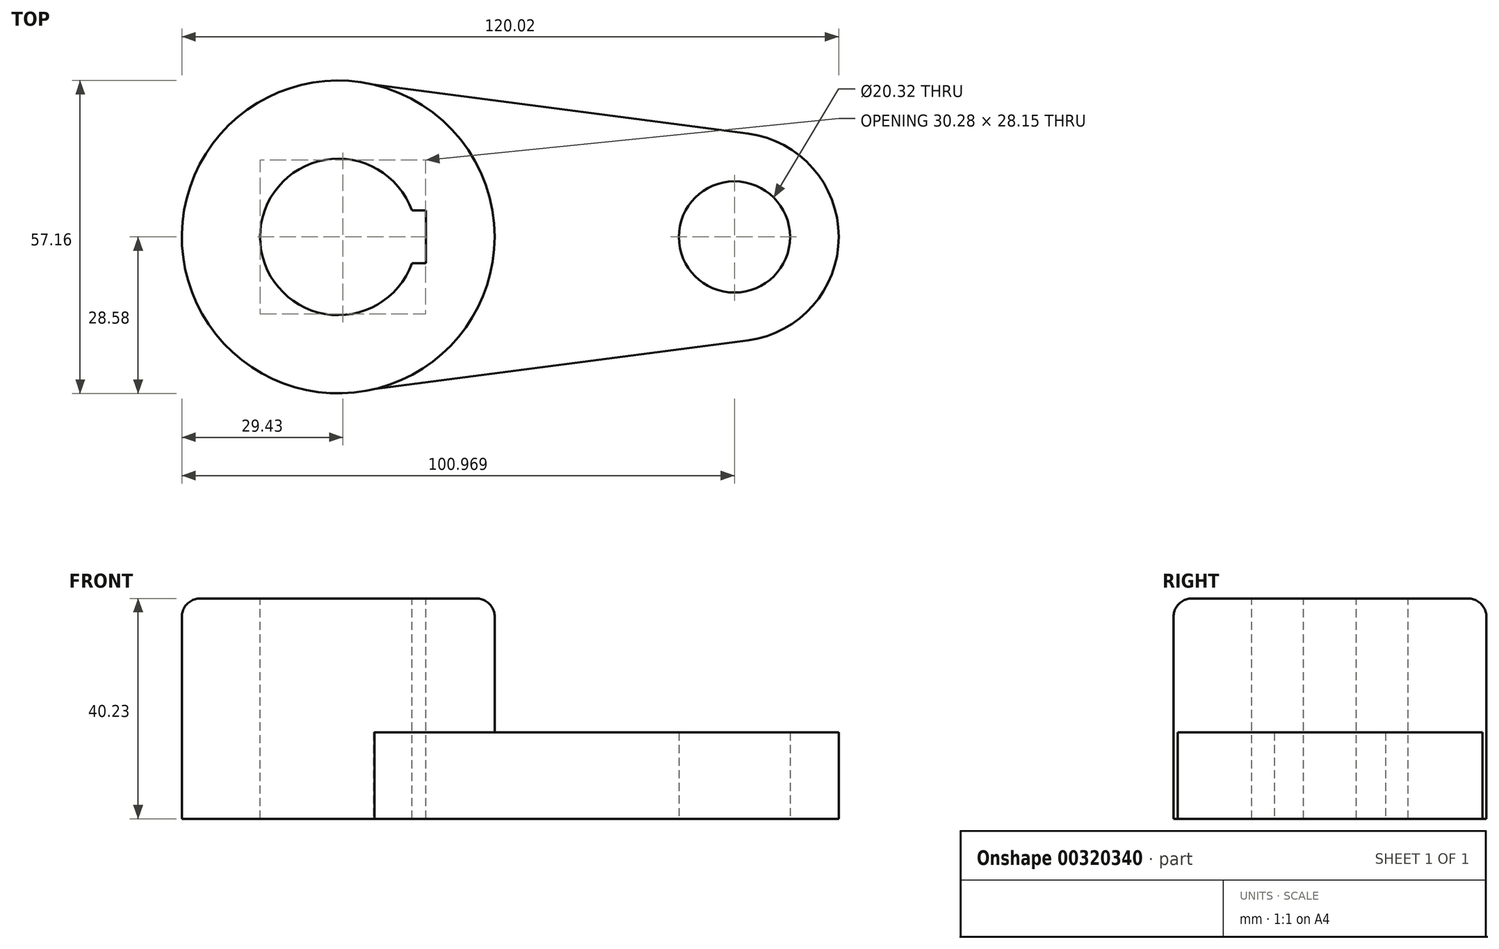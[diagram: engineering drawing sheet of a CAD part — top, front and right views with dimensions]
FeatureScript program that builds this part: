
annotation { "Feature Type Name" : "Feature", "Feature Type Description" : "" }
export const myFeature = defineFeature(function(context is Context, id is Id, definition is map)
    precondition{}
    {
        {
            var Q0;
            Q0=qCreatedBy(makeId("Top.planeOp"),FACE);
            var sketch = newSketch(context, id + "F0", { "sketchPlane" : qUnion([Q0])});
            skCircle(sketch, "E0", {"center": v(41.53, 0) * mm, "radius": 19.05 * mm});
            skCircle(sketch, "E1", {"center": v(-30.86, 0) * mm, "radius": 28.58 * mm});
            skLineSegment(sketch, "E2", {"start": v(-29.88, 28.56) * mm, "end": v(44, 18.89) * mm});
            skLineSegment(sketch, "E3", {"start": v(-30.11, -28.57) * mm, "end": v(44, -18.89) * mm});
            skSolve(sketch);
        }
        {
            var Q0;
            Q0 = qSketchRegion(id + "F0", true);
            extrude(context, id + "F1", {"entities" : qUnion([Q0]), "depth" : 15.77 * mm});
        }
        {
            var Q0;
            Q0=qCreatedBy(makeId("Top.planeOp"),FACE);
            var sketch = newSketch(context, id + "F2", { "sketchPlane" : qUnion([Q0])});
            skArc(sketch, "E4.0", {"start": v(-24.46, 27.85) * mm, "mid": v(-59.44, -0.1) * mm, "end": v(-24.25, -27.8) * mm});
            skArc(sketch, "E5.0.0", {"start": v(44, -18.89) * mm, "mid": v(60.58, 0) * mm, "end": v(44, 18.89) * mm, "construction": true});
            skLineSegment(sketch, "E5.0.1", {"start": v(44, 18.89) * mm, "end": v(-24.46, 27.85) * mm, "construction": true});
            skArc(sketch, "E5.0.2", {"start": v(-24.46, 27.85) * mm, "mid": v(-59.44, -0.1) * mm, "end": v(-24.25, -27.8) * mm, "construction": true});
            skLineSegment(sketch, "E5.0.3", {"start": v(-24.25, -27.8) * mm, "end": v(44, -18.89) * mm, "construction": true});
            skCircle(sketch, "E6", {"center": v(-30.86, 0) * mm, "radius": 28.57 * mm});
            skSolve(sketch);
        }
        {
            var Q0;
            Q0 = qSketchRegion(id + "F2", true);
            extrude(context, id + "F3", {"entities" : qUnion([Q0]), "operationType" : NewBodyOperationType.ADD, "depth" : 40.23 * mm});
        }
        {
            var Q0;
            Q0=makeQuery(id+"F3.opExtrude","CAP_EDGE",EDGE,{"disambiguationData":[OSD([sQuery(id+"F2.wireOp",EDGE,"E6")])],"isStart":false});
            fillet(context, id + "F4", {"entities" : qUnion([Q0]), "radius" : 3.3 * mm, "tangentPropagation" : true, "allowEdgeOverflow" : false});
        }
        {
            var Q0;
            Q0=qCreatedBy(makeId("Top.planeOp"),FACE);
            var sketch = newSketch(context, id + "F5", { "sketchPlane" : qUnion([Q0])});
            skArc(sketch, "E7.0", {"start": v(44, -18.89) * mm, "mid": v(60.58, 0) * mm, "end": v(44, 18.89) * mm, "construction": true});
            skCircle(sketch, "E8", {"center": v(41.53, 0) * mm, "radius": 10.16 * mm});
            skSolve(sketch);
        }
        {
            var Q0;
            Q0 = qSketchRegion(id + "F5", true);
            extrude(context, id + "F6", {"entities" : qUnion([Q0]), "operationType" : NewBodyOperationType.REMOVE, "endBound" : BoundingType.THROUGH_ALL, "depth" : 25.4 * mm});
        }
        {
            var Q0;
            Q0=makeQuery(id+"F3.opExtrude","CAP_FACE",FACE,{"disambiguationData":[OSD([sQuery(id+"F2.wireOp",EDGE,"E6")])],"isStart":false});
            var sketch = newSketch(context, id + "F7", { "sketchPlane" : qUnion([Q0])});
            skCircle(sketch, "E9.0.0", {"center": v(-30.86, 0) * mm, "radius": 25.27 * mm, "construction": true});
            skCircle(sketch, "E10", {"center": v(-30.86, 0) * mm, "radius": 14.29 * mm});
            skLineSegment(sketch, "E11.bottom", {"start": v(-14.87, 4.83) * mm, "end": v(-17.41, 4.83) * mm});
            skLineSegment(sketch, "E11.top", {"start": v(-14.87, -4.83) * mm, "end": v(-17.41, -4.83) * mm});
            skLineSegment(sketch, "E11.left", {"start": v(-14.87, 4.83) * mm, "end": v(-14.87, -4.83) * mm});
            skPoint(sketch, "E11.middle", {"position": v(-16.57, 0) * mm});
            skPoint(sketch, "E12.orphan", {"position": v(-18.28, 4.83) * mm});
            skPoint(sketch, "E13.orphan", {"position": v(-18.28, -4.83) * mm});
            skSolve(sketch);
        }
        {
            var Q0;
            Q0 = qSketchRegion(id + "F7", true);
            extrude(context, id + "F8", {"entities" : qUnion([Q0]), "operationType" : NewBodyOperationType.REMOVE, "endBound" : BoundingType.THROUGH_ALL, "oppositeDirection" : true, "depth" : 25.4 * mm});
        }
    });
